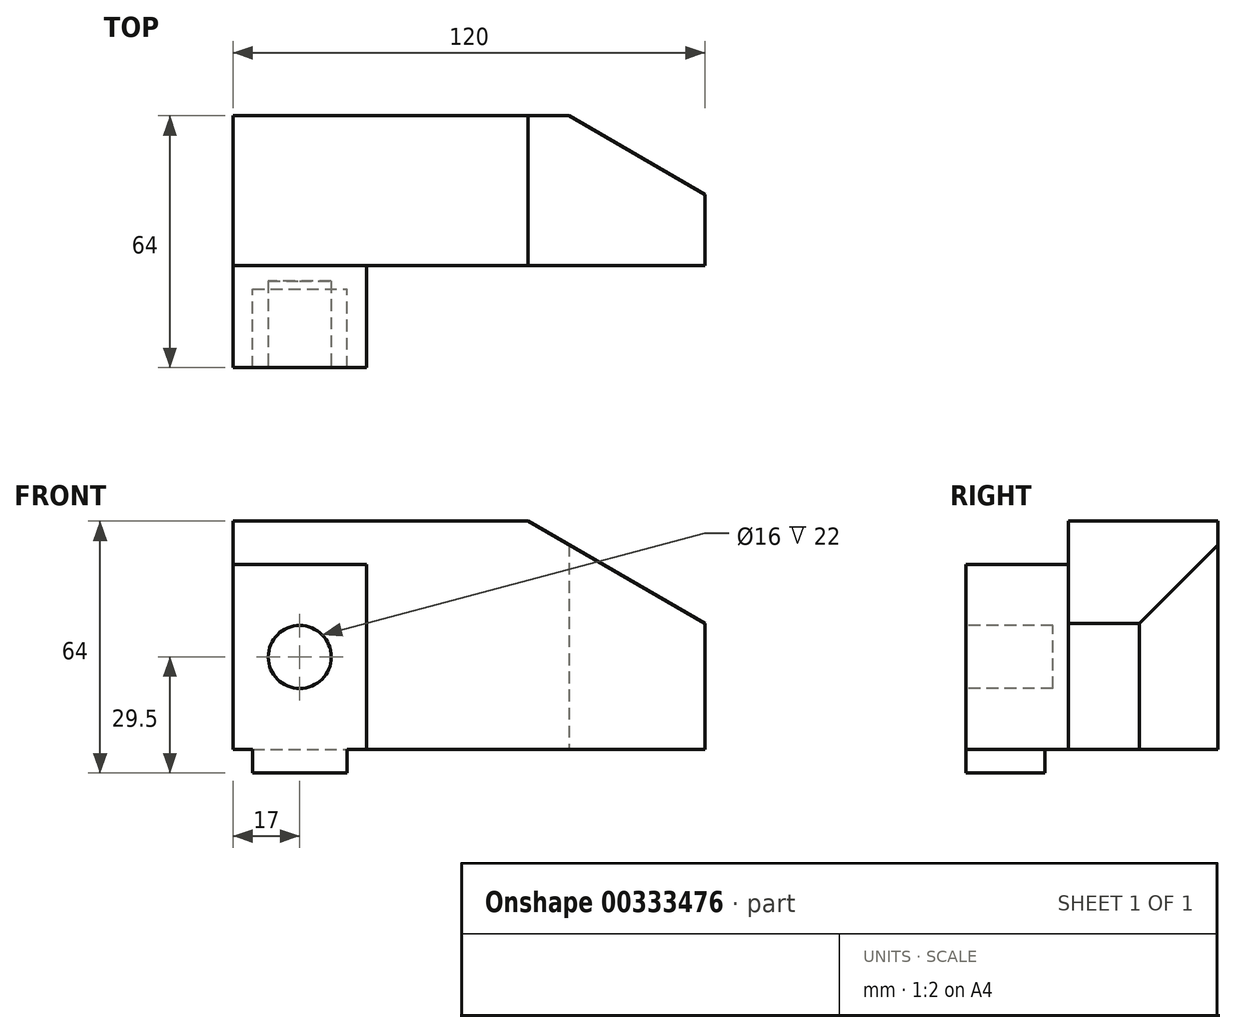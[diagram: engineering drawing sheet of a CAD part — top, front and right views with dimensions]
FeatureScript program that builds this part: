
annotation { "Feature Type Name" : "Feature", "Feature Type Description" : "" }
export const myFeature = defineFeature(function(context is Context, id is Id, definition is map)
    precondition{}
    {
        {
            var Q0;
            Q0=qCreatedBy(makeId("Top.planeOp"),FACE);
            var sketch = newSketch(context, id + "F0", { "sketchPlane" : qUnion([Q0])});
            skLineSegment(sketch, "E0", {"start": v(0, 0) * mm, "end": v(0, 38) * mm});
            skLineSegment(sketch, "E1", {"start": v(0, 38) * mm, "end": v(85.36, 38) * mm});
            skLineSegment(sketch, "E2", {"start": v(85.36, 38) * mm, "end": v(120, 18) * mm});
            skLineSegment(sketch, "E3", {"start": v(120, 18) * mm, "end": v(120, 0) * mm});
            skLineSegment(sketch, "E4", {"start": v(120, 0) * mm, "end": v(0, 0) * mm});
            skLineSegment(sketch, "E5", {"start": v(75, 38) * mm, "end": v(75, 0) * mm});
            skLineSegment(sketch, "E6", {"start": v(0, 0) * mm, "end": v(0, -16) * mm});
            skLineSegment(sketch, "E7", {"start": v(0, -16) * mm, "end": v(34, -16) * mm});
            skLineSegment(sketch, "E8", {"start": v(34, -16) * mm, "end": v(34, 0) * mm});
            skLineSegment(sketch, "E9", {"start": v(0, 0) * mm, "end": v(34, 0) * mm});
            skSolve(sketch);
        }
        {
            var Q0;
            Q0 = qSketchRegion(id + "F0", true);
            extrude(context, id + "F1", {"entities" : qUnion([Q0]), "depth" : 58 * mm});
        }
        {
            var Q0;
            Q0=makeQuery(id+"F1.opExtrude","SWEPT_FACE",FACE,{"disambiguationData":[OSD([sQuery(id+"F0.wireOp",EDGE,"E4")])]});
            var sketch = newSketch(context, id + "F2", { "sketchPlane" : qUnion([Q0])});
            skLineSegment(sketch, "E10", {"start": v(120, 32.02) * mm, "end": v(120, 58) * mm});
            skLineSegment(sketch, "E11", {"start": v(120, 58) * mm, "end": v(75, 58) * mm});
            skLineSegment(sketch, "E12", {"start": v(34, 58) * mm, "end": v(75, 58) * mm});
            skLineSegment(sketch, "E13", {"start": v(75, 58) * mm, "end": v(120, 32.02) * mm});
            skLineSegment(sketch, "E14", {"start": v(120, 0) * mm, "end": v(34, 0) * mm});
            skLineSegment(sketch, "E15", {"start": v(34, 0) * mm, "end": v(34, 58) * mm});
            skSolve(sketch);
        }
        {
            var Q0;
            Q0=makeQuery(id+"F2.imprint","IMPRINT",FACE,{"disambiguationData":[TD([[makeQuery(id+"F2.imprint","IMPRINT",EDGE,{"derivedFrom":sQuery(id+"F2.wireOp",EDGE,"E10")}),-1.0]])]});
            extrude(context, id + "F3", {"entities" : qUnion([Q0]), "operationType" : NewBodyOperationType.REMOVE, "endBound" : BoundingType.THROUGH_ALL, "oppositeDirection" : true, "depth" : 25 * mm});
        }
        {
            var Q0;
            Q0=makeQuery(id+"F1.opExtrude","SWEPT_FACE",FACE,{"disambiguationData":[OSD([sQuery(id+"F0.wireOp",EDGE,"E7")])]});
            var sketch = newSketch(context, id + "F4", { "sketchPlane" : qUnion([Q0])});
            skLineSegment(sketch, "E16", {"start": v(0, 47) * mm, "end": v(34, 47) * mm});
            skLineSegment(sketch, "E17", {"start": v(34, 47) * mm, "end": v(34, 58) * mm});
            skLineSegment(sketch, "E18", {"start": v(34, 58) * mm, "end": v(0, 58) * mm});
            skLineSegment(sketch, "E19", {"start": v(0, 58) * mm, "end": v(0, 47) * mm});
            skSolve(sketch);
        }
        {
            var Q0;
            Q0=makeQuery(id+"F4.imprint","IMPRINT",FACE,{"disambiguationData":[TD([[makeQuery(id+"F4.imprint","IMPRINT",EDGE,{"derivedFrom":sQuery(id+"F4.wireOp",EDGE,"E16")}),1.0]])]});
            extrude(context, id + "F5", {"entities" : qUnion([Q0]), "operationType" : NewBodyOperationType.REMOVE, "endBound" : BoundingType.SYMMETRIC, "oppositeDirection" : true, "depth" : 32 * mm});
        }
        {
            var Q0;
            Q0=makeQuery(id+"F1.opExtrude","SWEPT_FACE",FACE,{"disambiguationData":[OSD([sQuery(id+"F0.wireOp",EDGE,"E7")])]});
            var sketch = newSketch(context, id + "F6", { "sketchPlane" : qUnion([Q0])});
            skLineSegment(sketch, "E20", {"start": v(0, 47) * mm, "end": v(34, 47) * mm});
            skLineSegment(sketch, "E21", {"start": v(34, 47) * mm, "end": v(34, 0) * mm});
            skLineSegment(sketch, "E22", {"start": v(34, 0) * mm, "end": v(29, 0) * mm});
            skLineSegment(sketch, "E23", {"start": v(29, 0) * mm, "end": v(29, -6) * mm});
            skLineSegment(sketch, "E24", {"start": v(29, -6) * mm, "end": v(5, -6) * mm});
            skLineSegment(sketch, "E25", {"start": v(5, -6) * mm, "end": v(5, 0) * mm});
            skLineSegment(sketch, "E26", {"start": v(5, 0) * mm, "end": v(0, 0) * mm});
            skLineSegment(sketch, "E27", {"start": v(0, 0) * mm, "end": v(0, 47) * mm});
            skSolve(sketch);
        }
        {
            var Q0;
            Q0 = qSketchRegion(id + "F6", true);
            extrude(context, id + "F7", {"entities" : qUnion([Q0]), "operationType" : NewBodyOperationType.ADD, "endBound" : BoundingType.SYMMETRIC, "depth" : 20 * mm});
        }
        {
            var Q0;
            Q0=makeQuery(id+"F7.opExtrude","CAP_FACE",FACE,{"disambiguationData":[OSD([sQuery(id+"F6.wireOp",EDGE,"E20"),sQuery(id+"F6.wireOp",EDGE,"E21"),sQuery(id+"F6.wireOp",EDGE,"E22"),sQuery(id+"F6.wireOp",EDGE,"E23"),sQuery(id+"F6.wireOp",EDGE,"E24"),sQuery(id+"F6.wireOp",EDGE,"E25"),sQuery(id+"F6.wireOp",EDGE,"E26"),sQuery(id+"F6.wireOp",EDGE,"E27")])],"isStart":false});
            var sketch = newSketch(context, id + "F8", { "sketchPlane" : qUnion([Q0])});
            skCircle(sketch, "E28", {"center": v(17, 23.5) * mm, "radius": 8 * mm});
            skPoint(sketch, "E28.centerSnap0", {"position": v(17, 47) * mm});
            skPoint(sketch, "E28.centerSnap1", {"position": v(34, 23.5) * mm});
            skSolve(sketch);
        }
        {
            var Q0;
            Q0 = qSketchRegion(id + "F8", true);
            extrude(context, id + "F9", {"entities" : qUnion([Q0]), "operationType" : NewBodyOperationType.REMOVE, "oppositeDirection" : true, "depth" : 22 * mm});
        }
    });
